# Revit family: AD-C81Tw
name_source: partatom
category: Communication Devices
revit_build: Autodesk Revit Architecture 2012 (Build: 20110309_2315(x64)
units: mm (PartAtom-declared; Revit-internal decimal feet)

## types (1)
- AD-C81Tw
    100V Taps = 60, 30, 15
    70V Taps = 60, 30, 15, 7.5
    Coverage Horizontal = 180.00°
    Coverage Vertical = 180.00°
    Default Elevation = 48"
    Depth = 14.8"
    Description = 8" Weather Resistant Subwoofer Loudspeaker element
    Enclosure Depth = 13.5"
    Enclosure Radius = 5.75"
    Grille Depth = 0.3"
    Grille Radius Base = 6.3"
    Grille Radius Extent = 4.37"
    Impedance = 8
    Manufacturer = QSC Audio Products, LLC
    Manufacturer URL = www.qscaudio.com
    Middle Depth = 1"
    Middle Radius = 5.75"
    Model = AD-C81Tw
    Power Handling = 100
    Product Documentation Link = http://media.qscaudio.com
    Product Page URL = http://www.qscaudio.com
    Regulatory Compliance = RoHS, UL1480, UL2043
    SPL Max = 112
    Sensitivity = 92
    URL = http://www.qscaudio.com
    Weight Dimensional (kg) = 12.7
    Weight Dimensional (lb) = 28
    Weight Product (kg) = 9.8
    Weight Product (lb) = 20
    Width = 12.6"

## geometry (parser evidence)
native form markers: Blend x3, Sweep x1
no freeform markers — native parametric forms only
